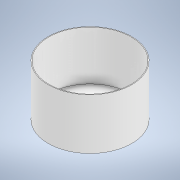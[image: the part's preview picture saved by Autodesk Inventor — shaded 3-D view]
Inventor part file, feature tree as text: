
AUTODESK INVENTOR PART (.ipt)
format: ipt  version: 2022 (Build 260153000, 153)  size: 126,464 bytes
history: native  units: in
note: dims shown in document units (in); Inventor stores cm internally (conversion verified against a paired STEP export)
features: extrude x2, sketch x2
ambient origin geometry x8: Origin, YZ Plane, XZ Plane, XY Plane, X Axis, Y Axis, Z Axis, Center Point
bodies: Body1 (feature_tree)
feature tree (4):
  extrude  "Extrusion2"  Depth=3.811in
  extrude  "Extrusion3"  Depth=2.2835in
  sketch  "Sketch2"  dims[d4=3.8819in d5=3.811in]
  sketch  "Sketch3"  dims[d6=2.3622in d7=0.0in d8=3.811in d9=2.2835in d10=0.0in]
